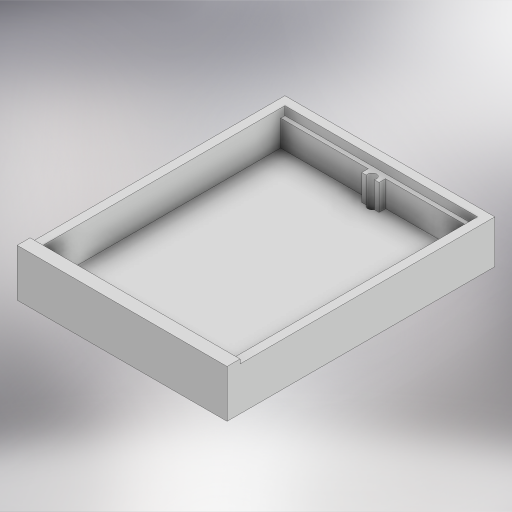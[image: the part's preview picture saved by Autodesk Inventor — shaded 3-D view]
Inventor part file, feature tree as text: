
AUTODESK INVENTOR PART (.ipt)
format: ipt  version: 2024 (Build 280153000, 153)  size: 331,776 bytes
history: native  units: in
note: dims shown in document units (in); Inventor stores cm internally (conversion verified against a paired STEP export)
features: sketch x6, extrude x5, hole x1
ambient origin geometry x8: Origin, YZ Plane, XZ Plane, XY Plane, X Axis, Y Axis, Z Axis, Center Point
bodies: Solid1 (feature_tree)
feature tree (12):
  extrude  "Extrusion1"  Depth=1.9134in
  extrude  "Extrusion2"  Depth=0.0787in
  extrude  "Extrusion3"  Depth=0.0787in TaperAngle=0.0deg
  extrude  "Extrusion4"  Depth=0.2362in TaperAngle=0.0deg
  extrude  "Extrusion5"  Depth=0.0394in
  hole  "Hole1"  [1 undecoded]
  sketch  "Sketch1"  dims[d0=2.4409in d1=1.9134in]
  sketch  "Sketch2"  dims[d2=0.3937in d3=0.0in d4=0.0787in]
  sketch  "Sketch3"  dims[d5=0.0787in d6=0.0787in d7=0.0in]
  sketch  "Sketch4"  dims[d8=0.0394in d9=0.2362in d10=0.0in]
  sketch  "Sketch6"  dims[d11=0.1181in d12=0.0394in]
  sketch  "Sketch7"  dims[d13=0.2362in d14=0.0in d15=0.1575in d16=0.0787in d17=0.0591in d18=0.3937in d19=0.0in d20=0.0827in d21=0.0787in d22=0.2362in d23=0.1575in d24=0.0787in d25=90.0deg d26=0.315in d27=0.8108in]
note: 1 required parameter value undecoded (feature->parameter linkage not recoverable at this tier; creation-order binding heuristic only, values carry confidence <= 0.55)
